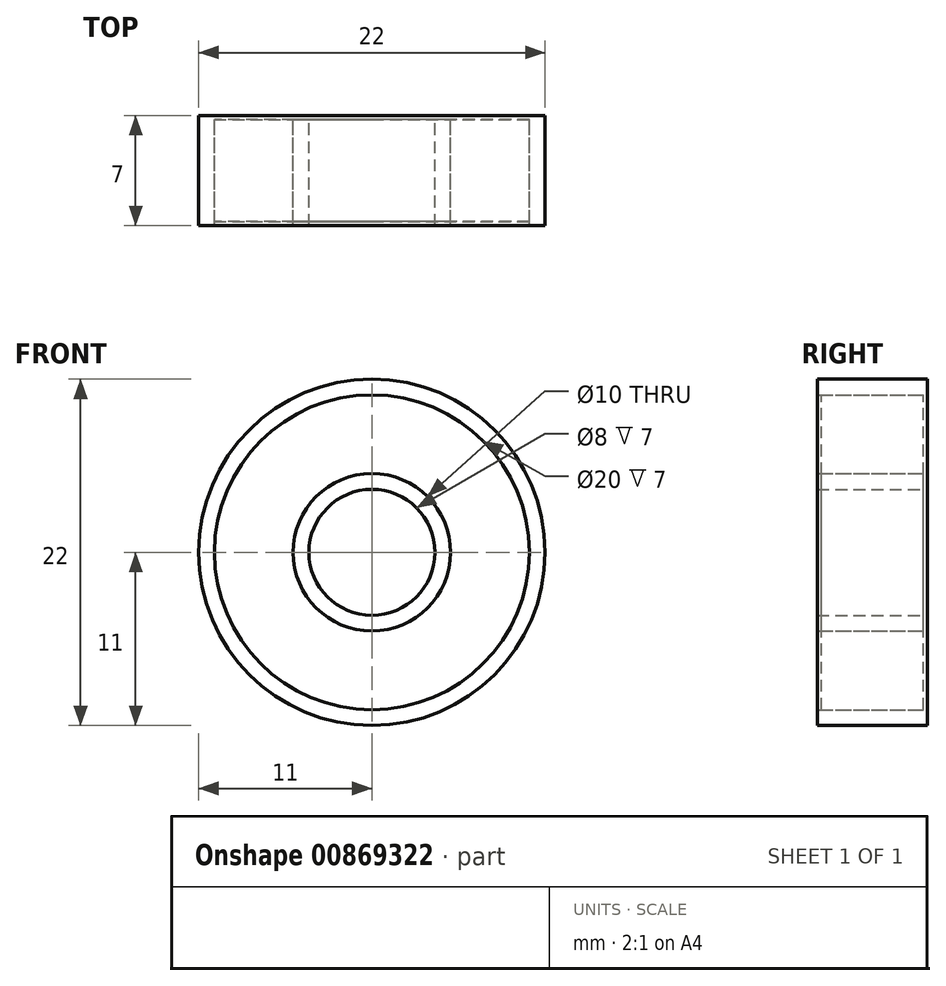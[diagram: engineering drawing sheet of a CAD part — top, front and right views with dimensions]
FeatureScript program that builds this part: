
annotation { "Feature Type Name" : "Feature", "Feature Type Description" : "" }
export const myFeature = defineFeature(function(context is Context, id is Id, definition is map)
    precondition{}
    {
        {
            var Q0;
            Q0=qCreatedBy(makeId("Front.planeOp"),FACE);
            var sketch = newSketch(context, id + "F0", { "sketchPlane" : qUnion([Q0])});
            skCircle(sketch, "E0", {"center": v(0, 0) * mm, "radius": 4 * mm});
            skCircle(sketch, "E1", {"center": v(0, 0) * mm, "radius": 5 * mm});
            skCircle(sketch, "E2", {"center": v(0, 0) * mm, "radius": 11 * mm});
            skCircle(sketch, "E3", {"center": v(0, 0) * mm, "radius": 10 * mm});
            skSolve(sketch);
        }
        {
            var Q0;
            Q0=makeQuery(id+"F0.imprint","IMPRINT",FACE,{"disambiguationData":[TD([[makeQuery(id+"F0.imprint","IMPRINT",EDGE,{"derivedFrom":sQuery(id+"F0.wireOp",EDGE,"E0")}),-1.0]])]});
            var Q1;
            Q1=makeQuery(id+"F0.imprint","IMPRINT",FACE,{"disambiguationData":[TD([[makeQuery(id+"F0.imprint","IMPRINT",EDGE,{"derivedFrom":sQuery(id+"F0.wireOp",EDGE,"E2")}),1.0]])]});
            extrude(context, id + "F1", {"entities" : qUnion([Q0, Q1]), "endBound" : BoundingType.SYMMETRIC, "depth" : 7 * mm, "offsetDistance" : 25.4 * mm});
        }
        {
            var Q0;
            Q0=makeQuery(id+"F0.imprint","IMPRINT",FACE,{"disambiguationData":[TD([[makeQuery(id+"F0.imprint","IMPRINT",EDGE,{"derivedFrom":sQuery(id+"F0.wireOp",EDGE,"E1")}),-1.0]])]});
            extrude(context, id + "F2", {"entities" : qUnion([Q0]), "endBound" : BoundingType.SYMMETRIC, "depth" : 6.5 * mm, "offsetDistance" : 25.4 * mm});
        }
    });
